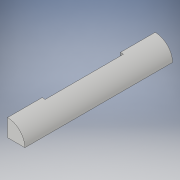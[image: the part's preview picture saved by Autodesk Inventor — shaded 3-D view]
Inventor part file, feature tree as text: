
AUTODESK INVENTOR PART (.ipt)
format: ipt  version: 2019.1 (Build 231200000, 200)  size: 108,544 bytes
history: native  units: in
note: dims shown in document units (in); Inventor stores cm internally (conversion verified against a paired STEP export)
features: extrude x2, sketch x2
ambient origin geometry x8: Origin, YZ Plane, XZ Plane, XY Plane, X Axis, Y Axis, Z Axis, Center Point
bodies: Solid1 (feature_tree)
feature tree (4):
  extrude  "Extrusion1"  Depth=6.375in TaperAngle=0.0deg
  extrude  "Extrusion2"  Depth=1.5in
  sketch  "Sketch1"  dims[d0=1.5in d1=6.375in d2=0.0in]
  sketch  "Sketch2"  dims[d3=3.375in d4=1.5in d5=0.125in d6=0.0in d7=0.0in]
